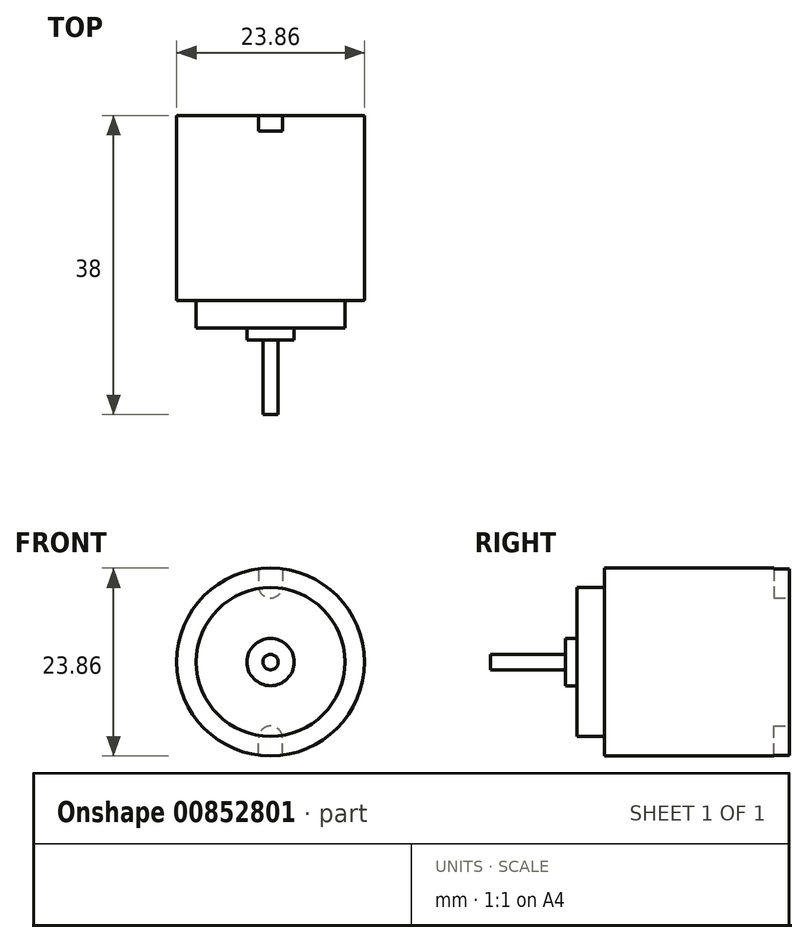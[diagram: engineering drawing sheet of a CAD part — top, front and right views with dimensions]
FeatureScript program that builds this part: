
annotation { "Feature Type Name" : "Feature", "Feature Type Description" : "" }
export const myFeature = defineFeature(function(context is Context, id is Id, definition is map)
    precondition{}
    {
        {
            var Q0;
            Q0=qCreatedBy(makeId("Right.planeOp"),FACE);
            var sketch = newSketch(context, id + "F0", { "sketchPlane" : qUnion([Q0])});
            skLineSegment(sketch, "E0", {"start": v(0, 0) * mm, "end": v(-47.82, 0) * mm, "construction": true});
            skLineSegment(sketch, "E1", {"start": v(0, 0) * mm, "end": v(-38, 0) * mm});
            skLineSegment(sketch, "E2", {"start": v(-38, 0) * mm, "end": v(-38, 0.97) * mm});
            skLineSegment(sketch, "E3", {"start": v(-38, 0.97) * mm, "end": v(-28.5, 0.97) * mm});
            skLineSegment(sketch, "E4", {"start": v(-28.5, 0.97) * mm, "end": v(-28.5, 3) * mm});
            skLineSegment(sketch, "E5", {"start": v(-28.5, 3) * mm, "end": v(-27, 3) * mm});
            skLineSegment(sketch, "E6", {"start": v(-27, 3) * mm, "end": v(-27, 9.45) * mm});
            skLineSegment(sketch, "E7", {"start": v(-27, 9.45) * mm, "end": v(-23.5, 9.45) * mm});
            skLineSegment(sketch, "E8", {"start": v(-23.5, 9.45) * mm, "end": v(-23.5, 11.92) * mm});
            skLineSegment(sketch, "E9", {"start": v(-23.5, 11.93) * mm, "end": v(0, 11.93) * mm});
            skLineSegment(sketch, "E10", {"start": v(0, 11.92) * mm, "end": v(0, 0) * mm});
            skSolve(sketch);
        }
        {
            var Q0;
            Q0 = qSketchRegion(id + "F0", true);
            var Q1;
            Q1=sQuery(id+"F0.wireOp",EDGE,"E0");
            revolve(context, id + "F1", {"surfaceOperationType" : NewSurfaceOperationType.NEW, "entities" : qUnion([Q0]), "axis" : qUnion([Q1]), "revolveType" : RevolveType.FULL});
        }
        {
            var Q0;
            Q0=makeQuery(id+"F1.opRevolve","SWEPT_FACE",FACE,{"disambiguationData":[OSD([sQuery(id+"F0.wireOp",EDGE,"E10")])]});
            var sketch = newSketch(context, id + "F2", { "sketchPlane" : qUnion([Q0])});
            skLineSegment(sketch, "E11.bottom", {"start": v(-1.5, 11.92) * mm, "end": v(1.5, 11.92) * mm});
            skLineSegment(sketch, "E11.top", {"start": v(-1.5, 9.62) * mm, "end": v(1.5, 9.62) * mm, "construction": true});
            skLineSegment(sketch, "E11.left", {"start": v(-1.5, 11.92) * mm, "end": v(-1.5, 9.62) * mm});
            skLineSegment(sketch, "E11.right", {"start": v(1.5, 11.92) * mm, "end": v(1.5, 9.62) * mm});
            skLineSegment(sketch, "E12", {"start": v(0, 0) * mm, "end": v(0, 9.62) * mm});
            skArc(sketch, "E13", {"start": v(-1.5, 9.62) * mm, "mid": v(0, 8.12) * mm, "end": v(1.5, 9.62) * mm});
            skArc(sketch, "E14.1.0", {"start": v(1.5, -9.62) * mm, "mid": v(0, -8.12) * mm, "end": v(-1.5, -9.62) * mm});
            skLineSegment(sketch, "E14.1.1", {"start": v(1.5, -11.93) * mm, "end": v(-1.5, -11.93) * mm});
            skLineSegment(sketch, "E14.1.2", {"start": v(-1.5, -11.92) * mm, "end": v(-1.5, -9.62) * mm});
            skLineSegment(sketch, "E14.1.3", {"start": v(1.5, -11.92) * mm, "end": v(1.5, -9.62) * mm});
            skPoint(sketch, "E14.center", {"position": v(0, 0) * mm});
            skSolve(sketch);
        }
        {
            var Q0;
            Q0 = qSketchRegion(id + "F2", true);
            extrude(context, id + "F3", {"entities" : qUnion([Q0]), "operationType" : NewBodyOperationType.REMOVE, "oppositeDirection" : true, "depth" : 2 * mm, "offsetDistance" : 25 * mm});
        }
    });
